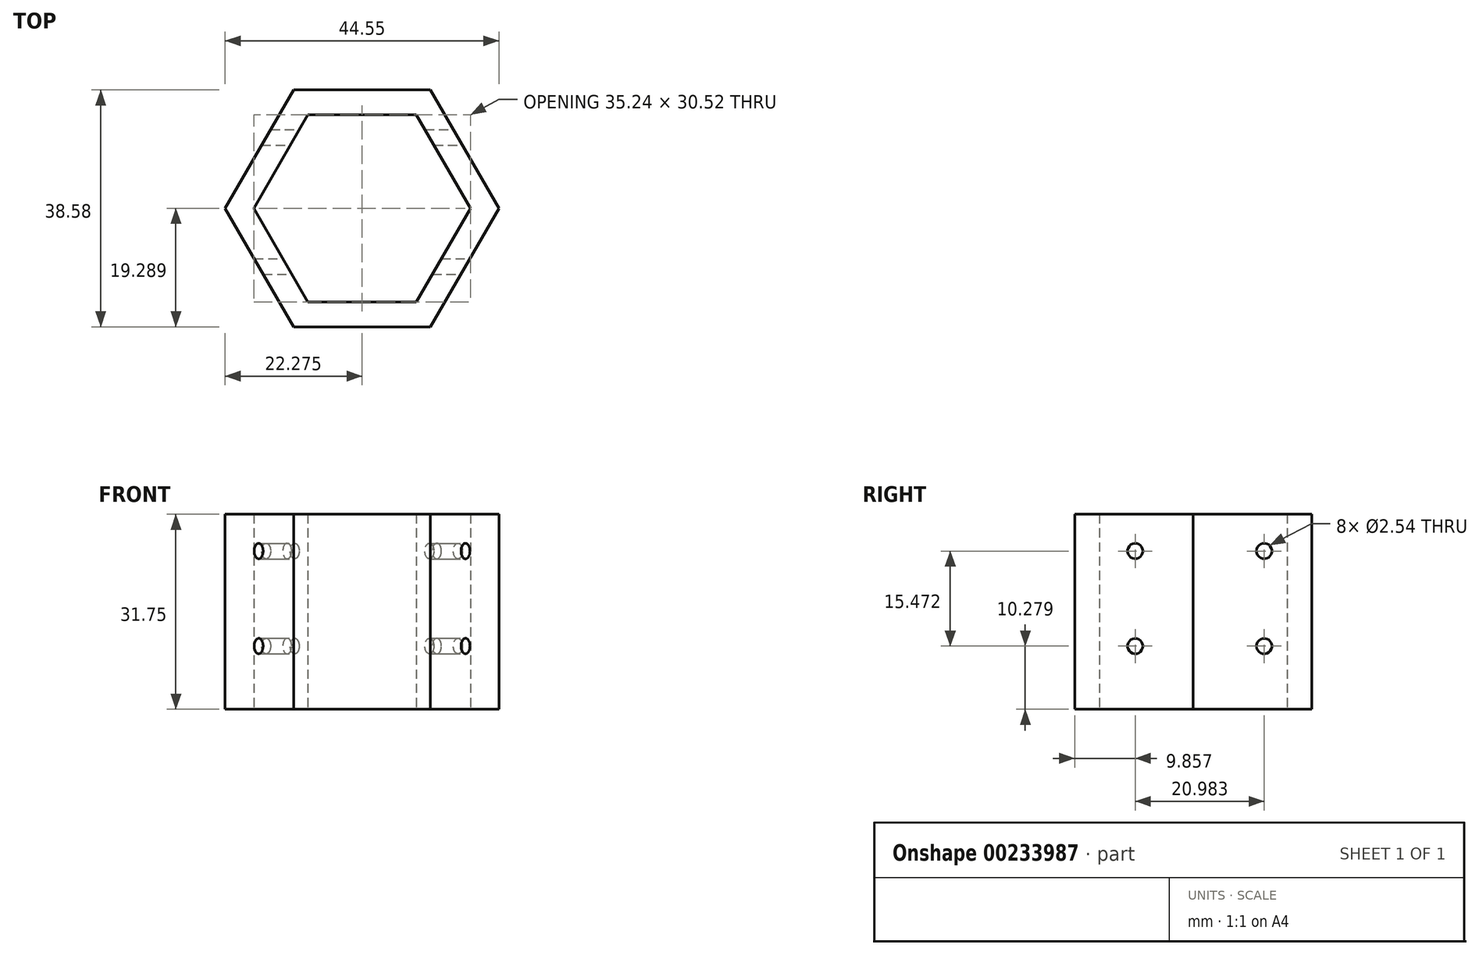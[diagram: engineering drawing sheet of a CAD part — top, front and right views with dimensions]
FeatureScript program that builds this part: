
annotation { "Feature Type Name" : "Feature", "Feature Type Description" : "" }
export const myFeature = defineFeature(function(context is Context, id is Id, definition is map)
    precondition{}
    {
        {
            var Q0;
            Q0=qCreatedBy(makeId("Top.planeOp"),FACE);
            var sketch = newSketch(context, id + "F0", { "sketchPlane" : qUnion([Q0])});
            skCircle(sketch, "E0.cCircle", {"center": v(-19.08, 20.03) * mm, "radius": 19.29 * mm, "construction": true});
            skLineSegment(sketch, "E0.0", {"start": v(-30.21, 39.32) * mm, "end": v(-7.94, 39.32) * mm});
            skLineSegment(sketch, "E0.1", {"start": v(-7.94, 39.32) * mm, "end": v(3.2, 20.03) * mm});
            skLineSegment(sketch, "E0.2", {"start": v(3.2, 20.03) * mm, "end": v(-7.94, 0.74) * mm});
            skLineSegment(sketch, "E0.3", {"start": v(-7.94, 0.74) * mm, "end": v(-30.21, 0.74) * mm});
            skLineSegment(sketch, "E0.4", {"start": v(-30.21, 0.74) * mm, "end": v(-41.35, 20.03) * mm});
            skLineSegment(sketch, "E0.5", {"start": v(-41.35, 20.03) * mm, "end": v(-30.21, 39.32) * mm});
            skPoint(sketch, "E0.0.midPoint", {"position": v(-19.08, 39.32) * mm});
            skCircle(sketch, "E1.cCircle", {"center": v(-19.08, 20.03) * mm, "radius": 15.26 * mm, "construction": true});
            skLineSegment(sketch, "E1.0", {"start": v(-27.89, 35.29) * mm, "end": v(-10.26, 35.29) * mm});
            skLineSegment(sketch, "E1.1", {"start": v(-10.26, 35.29) * mm, "end": v(-1.45, 20.03) * mm});
            skLineSegment(sketch, "E1.2", {"start": v(-1.45, 20.03) * mm, "end": v(-10.26, 4.77) * mm});
            skLineSegment(sketch, "E1.3", {"start": v(-10.26, 4.77) * mm, "end": v(-27.89, 4.77) * mm});
            skLineSegment(sketch, "E1.4", {"start": v(-27.89, 4.77) * mm, "end": v(-36.7, 20.03) * mm});
            skLineSegment(sketch, "E1.5", {"start": v(-36.7, 20.03) * mm, "end": v(-27.89, 35.29) * mm});
            skPoint(sketch, "E1.0.midPoint", {"position": v(-19.08, 35.29) * mm});
            skCircle(sketch, "E2.cCircle", {"center": v(-19.08, 20.03) * mm, "radius": 8.69 * mm, "construction": true});
            skLineSegment(sketch, "E2.0", {"start": v(-24.1, 28.72) * mm, "end": v(-14.06, 28.72) * mm});
            skLineSegment(sketch, "E2.1", {"start": v(-14.06, 28.72) * mm, "end": v(-9.04, 20.03) * mm});
            skLineSegment(sketch, "E2.2", {"start": v(-9.04, 20.03) * mm, "end": v(-14.06, 11.34) * mm});
            skLineSegment(sketch, "E2.3", {"start": v(-14.06, 11.34) * mm, "end": v(-24.1, 11.34) * mm});
            skLineSegment(sketch, "E2.4", {"start": v(-24.1, 11.34) * mm, "end": v(-29.1, 20.03) * mm});
            skLineSegment(sketch, "E2.5", {"start": v(-29.1, 20.03) * mm, "end": v(-24.1, 28.72) * mm});
            skPoint(sketch, "E2.0.midPoint", {"position": v(-19.08, 28.72) * mm});
            skSolve(sketch);
        }
        {
            var Q0;
            Q0 = qSketchRegion(id + "F0", true);
            extrude(context, id + "F1", {"entities" : qUnion([Q0]), "depth" : 31.75 * mm});
        }
        {
            var Q0;
            Q0=qCreatedBy(makeId("Right.planeOp"),FACE);
            var sketch = newSketch(context, id + "F2", { "sketchPlane" : qUnion([Q0])});
            skPoint(sketch, "E3", {"position": v(31.58, 10.28) * mm});
            skPoint(sketch, "E4", {"position": v(10.6, 10.28) * mm});
            skPoint(sketch, "E5", {"position": v(10.6, 25.75) * mm});
            skPoint(sketch, "E6", {"position": v(31.58, 25.75) * mm});
            skSolve(sketch);
        }
        {
            var Q0;
            Q0=sQuery(id+"F2.wireOp",VERTEX,"E5");
            var Q1;
            Q1=sQuery(id+"F2.wireOp",VERTEX,"E6");
            var Q2;
            Q2=sQuery(id+"F2.wireOp",VERTEX,"E3");
            var Q3;
            Q3=sQuery(id+"F2.wireOp",VERTEX,"E4");
            var Q4;
            Q4=makeQuery(id+"F1.opExtrude","SWEPT_BODY",BODY,{"disambiguationData":[OSD([sQuery(id+"F0.wireOp",EDGE,"E0.0"),sQuery(id+"F0.wireOp",EDGE,"E0.1"),sQuery(id+"F0.wireOp",EDGE,"E0.2"),sQuery(id+"F0.wireOp",EDGE,"E0.3"),sQuery(id+"F0.wireOp",EDGE,"E0.4"),sQuery(id+"F0.wireOp",EDGE,"E0.5"),sQuery(id+"F0.wireOp",EDGE,"E1.0"),sQuery(id+"F0.wireOp",EDGE,"E1.1"),sQuery(id+"F0.wireOp",EDGE,"E1.2"),sQuery(id+"F0.wireOp",EDGE,"E1.3"),sQuery(id+"F0.wireOp",EDGE,"E1.4"),sQuery(id+"F0.wireOp",EDGE,"E1.5")])]});
            hole(context, id + "F3", {"style" : HoleStyle.SIMPLE, "endStyle" : HoleEndStyle.THROUGH, "holeDiameter" : 2.54 * mm, "locations" : qUnion([Q0, Q1, Q2, Q3]), "scope" : qUnion([Q4]), "isTappedThrough" : true});
        }
    });
